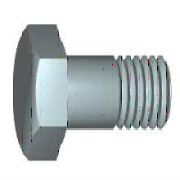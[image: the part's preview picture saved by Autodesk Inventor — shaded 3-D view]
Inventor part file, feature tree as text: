
AUTODESK INVENTOR PART (.ipt)
format: ipt  version: 2023.2 (Build 272271030, 271C)  size: 174,592 bytes
history: native  units: mm
features: sketch x2, revolve x1, thread x1, chamfer x1
ambient origin geometry x8: Origin, YZ Plane, XZ Plane, XY Plane, X Axis, Y Axis, Z Axis, Center Point
bodies: Solid1 (feature_tree)
feature tree (5):
  revolve  "Revolution1"  [1 undecoded]
  thread  "Thread1"  [1 undecoded]
  chamfer  "Chamfer1"  Distance=0.6mm
  sketch  "Sketch1"  dims[d0=19.5mm d1=8.0mm d3=30.0mm]
  sketch  "Sketch2"  dims[d4=11.5mm d5=0.6mm d6=90.0deg d14=22.0mm d15=0.0mm d16=0.666667mm d17=2.0mm d18=45.0deg d19=0.0mm d20=0.0mm d21=0.0mm d22=30.0deg d23=12.35mm d24=5.3mm d25=13.0mm d26=5.3mm d27=0.0mm]
note: 2 required parameter values undecoded (feature->parameter linkage not recoverable at this tier; creation-order binding heuristic only, values carry confidence <= 0.55)